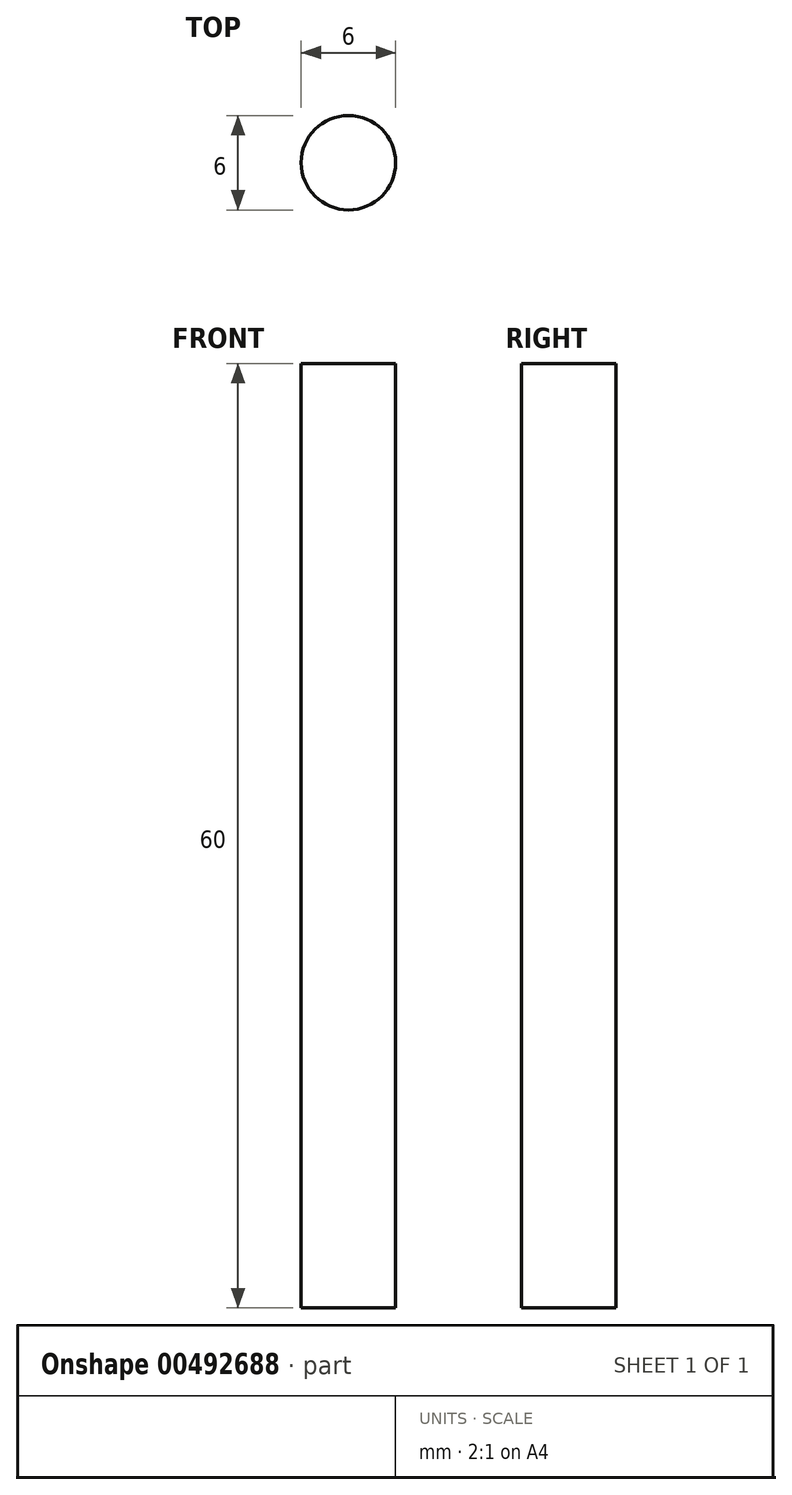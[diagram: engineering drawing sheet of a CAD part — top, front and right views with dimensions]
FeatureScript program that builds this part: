
annotation { "Feature Type Name" : "Feature", "Feature Type Description" : "" }
export const myFeature = defineFeature(function(context is Context, id is Id, definition is map)
    precondition{}
    {
        {
            var Q0;
            Q0=qCreatedBy(makeId("Top.planeOp"),FACE);
            var sketch = newSketch(context, id + "F0", { "sketchPlane" : qUnion([Q0])});
            skCircle(sketch, "E0", {"center": v(0, 0) * mm, "radius": 3 * mm});
            skSolve(sketch);
        }
        {
            var Q0;
            Q0 = qSketchRegion(id + "F0", true);
            extrude(context, id + "F1", {"entities" : qUnion([Q0]), "depth" : 60 * mm, "offsetDistance" : 25 * mm});
        }
    });
